# Revit family: Dämmauflage LK
name_source: partatom
category: HLS-Bauteile
units: mm (PartAtom-declared; Revit-internal decimal feet)

## family parameters
Arbeitsebenenbasiert = Ja
Beim Laden mit Abzugskörper schneiden = Nein
Bemaßung runder Anschluss = Durchmesser verwenden
Beschriftungsausrichtung beibehalten = Nein
Gemeinsam genutzt = Ja
Immer vertikal = Nein
Raumberechnungspunkt = Nein
Teiletyp = Normal

## types (3) — shared parameters
Dämmstärke = 13 mm
Fabrikat = MEFA
Farbe = Grau
Gewicht pro Bauteil = 0.00 kg
Gewicht pro Stück = 0.00 kg
H = 13 mm
Länge = 7000 mm
Material = Kautschuk
Materialname = geschlossenzelliger, synthetischer Kautschuk
Mengeneinheit = Beu
Stärke = 13 mm
Vorgabe-Ansicht = 1219 mm
Wärmeleitfähigkeit = 0.04 W/mK
max. Temperaturbeständigkeit = 105 °C
vpe = 1

## per-type parameters (varying)
| type | Artikelnummer | B | Breite | EAN | Gewicht | Kurztext1 | Kurztext2 |
| Dämmauflage LK, 45x13 | 7250045 | 45 mm  [stored 0.147638 ft] | 45 mm  [stored 0.147638 ft] | 4250928442109 | 0.24 kg | Schalldämmauflage C-Profil 45 | 7 m 45 mm Kautschuk |
| Dämmauflage LK, 35x13 | 7250035 | 35 mm  [stored 0.114829 ft] | 35 mm  [stored 0.114829 ft] | 4250928442093 | 0.20 kg | Schalldämmauflage C-Profil 35 | 7 m 35 mm Kautschuk |
| Dämmauflage LK, 25x13 | 7250025 | 25 mm  [stored 0.082021 ft] | 25 mm  [stored 0.082021 ft] | 4250928442086 | 0.13 kg | Schalldämmauflage C-Profil 27 | 7 m 25 mm Kautschuk |

note: [stored X ft] marks values corroborated as IEEE doubles in the binary element streams (Revit-internal decimal feet)
